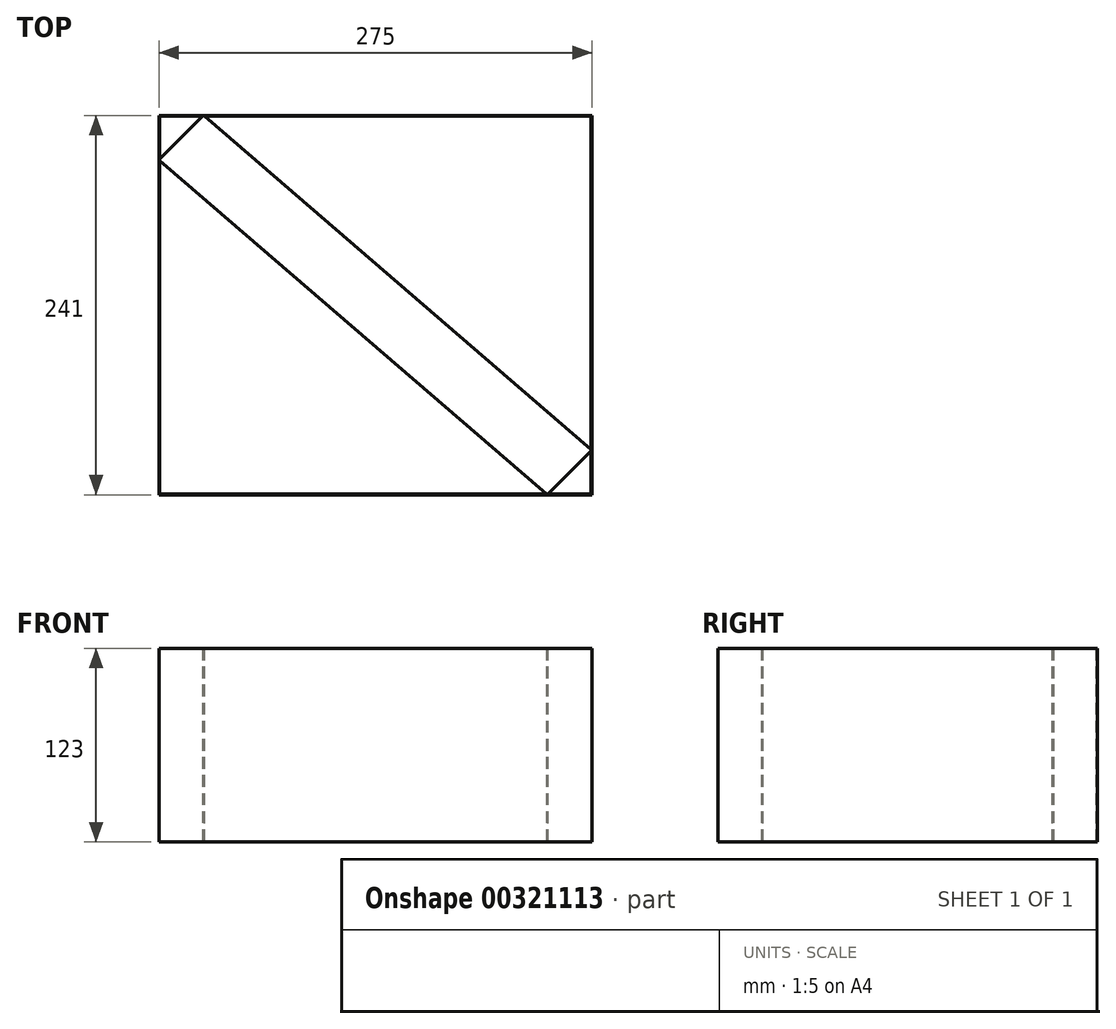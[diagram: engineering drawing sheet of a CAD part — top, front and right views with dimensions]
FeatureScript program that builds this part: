
annotation { "Feature Type Name" : "Feature", "Feature Type Description" : "" }
export const myFeature = defineFeature(function(context is Context, id is Id, definition is map)
    precondition{}
    {
        {
            var Q0;
            Q0=qCreatedBy(makeId("Front.planeOp"),FACE);
            var sketch = newSketch(context, id + "F0", { "sketchPlane" : qUnion([Q0])});
            skLineSegment(sketch, "E0", {"start": v(0, 0) * mm, "end": v(0, 123) * mm});
            skLineSegment(sketch, "E1", {"start": v(0, 123) * mm, "end": v(275, 123) * mm});
            skLineSegment(sketch, "E2", {"start": v(275, 123) * mm, "end": v(275, 0) * mm});
            skLineSegment(sketch, "E3", {"start": v(275, 0) * mm, "end": v(0, 0) * mm});
            skSolve(sketch);
        }
        {
            var Q0;
            Q0 = qSketchRegion(id + "F0", true);
            extrude(context, id + "F1", {"entities" : qUnion([Q0]), "depth" : 241 * mm});
        }
        {
            var Q0;
            Q0=makeQuery(id+"F1.opExtrude","SWEPT_FACE",FACE,{"disambiguationData":[OSD([sQuery(id+"F0.wireOp",EDGE,"E1")])]});
            var sketch = newSketch(context, id + "F2", { "sketchPlane" : qUnion([Q0])});
            skLineSegment(sketch, "E4", {"start": v(0, 0) * mm, "end": v(275, -241) * mm});
            skLineSegment(sketch, "E5", {"start": v(275, -241) * mm, "end": v(275, -212.7) * mm});
            skLineSegment(sketch, "E6", {"start": v(275, -241) * mm, "end": v(246.71, -241) * mm});
            skLineSegment(sketch, "E7", {"start": v(246.7, -241) * mm, "end": v(275, -212.7) * mm});
            skLineSegment(sketch, "E8", {"start": v(346.74, -130.94) * mm, "end": v(369.24, -105.26) * mm});
            skLineSegment(sketch, "E9", {"start": v(0, 0) * mm, "end": v(0, -28.29) * mm});
            skLineSegment(sketch, "E10", {"start": v(0, 0) * mm, "end": v(28.29, 0) * mm});
            skLineSegment(sketch, "E11", {"start": v(28.3, 0) * mm, "end": v(0, -28.3) * mm});
            skLineSegment(sketch, "E12", {"start": v(0, -28.29) * mm, "end": v(246.71, -241) * mm});
            skLineSegment(sketch, "E13", {"start": v(275, -212.71) * mm, "end": v(28.29, 0) * mm});
            skSolve(sketch);
        }
        {
            var Q0;
            Q0=makeQuery(id+"F1.opExtrude","SWEPT_FACE",FACE,{"disambiguationData":[OSD([sQuery(id+"F0.wireOp",EDGE,"E1")])]});
            shell(context, id + "F3", {"entities" : qUnion([Q0]), "thickness" : .5 * mm});
        }
        {
            var Q0;
            {var subQ5=sQuery(id+"F2.wireOp",EDGE,"E12");Q0=makeQuery(id+"F2.imprint","IMPRINT",FACE,{"disambiguationData":[TD([[makeQuery(id+"F2.imprint","IMPRINT",EDGE,{"derivedFrom":subQ5}),1.0]])]});}
            var Q1;
            {var subQ5=sQuery(id+"F2.wireOp",EDGE,"E13");Q1=makeQuery(id+"F2.imprint","IMPRINT",FACE,{"disambiguationData":[TD([[makeQuery(id+"F2.imprint","IMPRINT",EDGE,{"derivedFrom":subQ5}),1.0]])]});}
            extrude(context, id + "F4", {"entities" : qUnion([Q0, Q1]), "operationType" : NewBodyOperationType.ADD, "oppositeDirection" : true, "depth" : 122.9 * mm});
        }
    });
